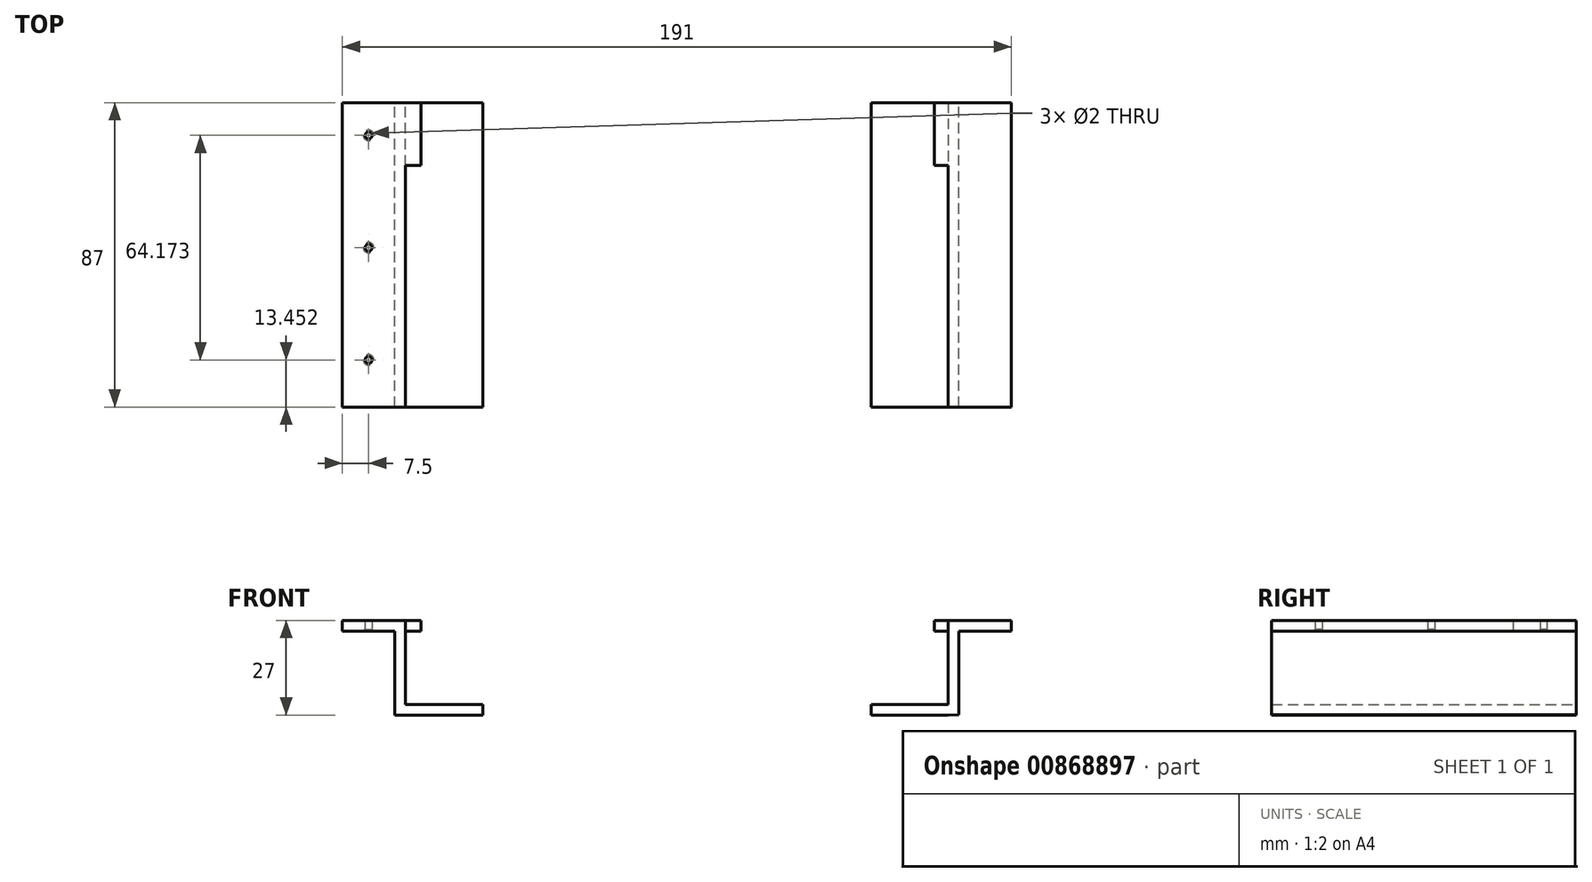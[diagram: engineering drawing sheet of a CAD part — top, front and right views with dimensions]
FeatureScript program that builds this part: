
annotation { "Feature Type Name" : "Feature", "Feature Type Description" : "" }
export const myFeature = defineFeature(function(context is Context, id is Id, definition is map)
    precondition{}
    {
        {
            var Q0;
            Q0=qCreatedBy(makeId("Front.planeOp"),FACE);
            var sketch = newSketch(context, id + "F0", { "sketchPlane" : qUnion([Q0])});
            skLineSegment(sketch, "E0", {"start": v(0, 0) * mm, "end": v(-77.5, 0) * mm});
            skLineSegment(sketch, "E1.bottom", {"start": v(-77.5, 0) * mm, "end": v(77.5, 0) * mm});
            skLineSegment(sketch, "E1.top", {"start": v(-77.5, 24) * mm, "end": v(77.5, 24) * mm});
            skLineSegment(sketch, "E1.left", {"start": v(-77.5, 0) * mm, "end": v(-77.5, 24) * mm});
            skLineSegment(sketch, "E1.right", {"start": v(77.5, 0) * mm, "end": v(77.5, 24) * mm});
            skLineSegment(sketch, "E2", {"start": v(-77.5, 24) * mm, "end": v(-80.5, 24) * mm});
            skLineSegment(sketch, "E3", {"start": v(-80.5, 24) * mm, "end": v(-80.5, 0) * mm});
            skLineSegment(sketch, "E4", {"start": v(-80.5, 0) * mm, "end": v(-80.5, -3) * mm});
            skLineSegment(sketch, "E5", {"start": v(-80.5, -3) * mm, "end": v(77.5, -3) * mm});
            skLineSegment(sketch, "E6", {"start": v(77.5, -3) * mm, "end": v(80.5, -2.98) * mm});
            skLineSegment(sketch, "E7", {"start": v(80.5, -2.98) * mm, "end": v(80.5, 24) * mm});
            skLineSegment(sketch, "E8", {"start": v(80.5, 24) * mm, "end": v(77.5, 24) * mm});
            skLineSegment(sketch, "E9", {"start": v(-80.5, 24) * mm, "end": v(-95.5, 24) * mm});
            skLineSegment(sketch, "E10", {"start": v(-95.5, 24) * mm, "end": v(-95.5, 21) * mm});
            skLineSegment(sketch, "E11", {"start": v(-95.5, 21) * mm, "end": v(-80.5, 21) * mm});
            skLineSegment(sketch, "E12", {"start": v(0, 24) * mm, "end": v(0, -47.67) * mm});
            skLineSegment(sketch, "E13.MirrorCS", {"start": v(77.5, 24) * mm, "end": v(80.5, 24) * mm});
            skLineSegment(sketch, "E14.MirrorCS", {"start": v(95.5, 24) * mm, "end": v(95.5, 21) * mm});
            skLineSegment(sketch, "E15.MirrorCS", {"start": v(80.5, 0) * mm, "end": v(80.5, -3) * mm});
            skLineSegment(sketch, "E16.MirrorCS", {"start": v(80.5, 24) * mm, "end": v(95.5, 24) * mm});
            skLineSegment(sketch, "E17.MirrorCS", {"start": v(80.5, 24) * mm, "end": v(80.5, 0) * mm});
            skLineSegment(sketch, "E18.MirrorCS", {"start": v(95.5, 21) * mm, "end": v(80.5, 21) * mm});
            skLineSegment(sketch, "E19", {"start": v(-77.5, 21) * mm, "end": v(-73, 21) * mm});
            skLineSegment(sketch, "E20", {"start": v(-73, 21) * mm, "end": v(-73, 24) * mm});
            skLineSegment(sketch, "E21", {"start": v(77.5, 21) * mm, "end": v(73.5, 21) * mm});
            skLineSegment(sketch, "E22", {"start": v(73.5, 21) * mm, "end": v(73.5, 24) * mm});
            skLineSegment(sketch, "E23", {"start": v(-95.5, 24) * mm, "end": v(-55.5, 24) * mm});
            skLineSegment(sketch, "E24", {"start": v(-55.44, 24.1) * mm, "end": v(-55.44, -3) * mm});
            skLineSegment(sketch, "E25", {"start": v(95.5, 24) * mm, "end": v(55.5, 24) * mm});
            skLineSegment(sketch, "E26", {"start": v(55.5, 24) * mm, "end": v(55.5, -3) * mm});
            skSolve(sketch);
        }
        {
            var Q0;
            {var subQ4=sQuery(id+"F0.wireOp",EDGE,"E10");Q0=makeQuery(id+"F0.imprint","IMPRINT",FACE,{"disambiguationData":[TD([[makeQuery(id+"F0.imprint","IMPRINT",EDGE,{"derivedFrom":subQ4}),1.0]])]});}
            var Q1;
            {var subQ11=sQuery(id+"F0.wireOp",EDGE,"E4");Q1=makeQuery(id+"F0.imprint","IMPRINT",FACE,{"disambiguationData":[TD([[makeQuery(id+"F0.imprint","IMPRINT",EDGE,{"derivedFrom":subQ11}),1.0]])]});}
            var Q2;
            {var subQ1=sQuery(id+"F0.wireOp",EDGE,"E6");Q2=makeQuery(id+"F0.imprint","IMPRINT",FACE,{"disambiguationData":[TD([[makeQuery(id+"F0.imprint","IMPRINT",EDGE,{"derivedFrom":subQ1}),1.0]])]});}
            var Q3;
            {var subQ0=sQuery(id+"F0.wireOp",EDGE,"E14.MirrorCS");Q3=makeQuery(id+"F0.imprint","IMPRINT",FACE,{"disambiguationData":[TD([[makeQuery(id+"F0.imprint","IMPRINT",EDGE,{"derivedFrom":subQ0}),-1.0]])]});}
            extrude(context, id + "F1", {"entities" : qUnion([Q0, Q1, Q2, Q3]), "depth" : 69 * mm, "offsetDistance" : 25 * mm});
        }
        {
            var Q0;
            {var subQ0=sQuery(id+"F0.wireOp",EDGE,"E14.MirrorCS");Q0=makeQuery(id+"F0.imprint","IMPRINT",FACE,{"disambiguationData":[TD([[makeQuery(id+"F0.imprint","IMPRINT",EDGE,{"derivedFrom":subQ0}),-1.0]])]});}
            var Q1;
            {var subQ3=sQuery(id+"F0.wireOp",EDGE,"E21");Q1=makeQuery(id+"F0.imprint","IMPRINT",FACE,{"disambiguationData":[TD([[makeQuery(id+"F0.imprint","IMPRINT",EDGE,{"derivedFrom":subQ3}),-1.0]])]});}
            var Q2;
            {var subQ1=sQuery(id+"F0.wireOp",EDGE,"E6");Q2=makeQuery(id+"F0.imprint","IMPRINT",FACE,{"disambiguationData":[TD([[makeQuery(id+"F0.imprint","IMPRINT",EDGE,{"derivedFrom":subQ1}),1.0]])]});}
            var Q3;
            {var subQ4=sQuery(id+"F0.wireOp",EDGE,"E10");Q3=makeQuery(id+"F0.imprint","IMPRINT",FACE,{"disambiguationData":[TD([[makeQuery(id+"F0.imprint","IMPRINT",EDGE,{"derivedFrom":subQ4}),1.0]])]});}
            var Q4;
            {var subQ3=sQuery(id+"F0.wireOp",EDGE,"E19");Q4=makeQuery(id+"F0.imprint","IMPRINT",FACE,{"disambiguationData":[TD([[makeQuery(id+"F0.imprint","IMPRINT",EDGE,{"derivedFrom":subQ3}),1.0]])]});}
            var Q5;
            {var subQ11=sQuery(id+"F0.wireOp",EDGE,"E4");Q5=makeQuery(id+"F0.imprint","IMPRINT",FACE,{"disambiguationData":[TD([[makeQuery(id+"F0.imprint","IMPRINT",EDGE,{"derivedFrom":subQ11}),1.0]])]});}
            extrude(context, id + "F2", {"entities" : qUnion([Q0, Q1, Q2, Q3, Q4, Q5]), "operationType" : NewBodyOperationType.ADD, "oppositeDirection" : true, "depth" : 18 * mm, "offsetDistance" : 25 * mm});
        }
        {
            var Q0;
            {var subQ0=sQuery(id+"F0.wireOp",EDGE,"E18.MirrorCS");Q0=makeQuery(id+"F2.boolean.opBoolean","MERGE",FACE,{"derivedFrom":[makeQuery(id+"F1.opExtrude","SWEPT_FACE",FACE,{"disambiguationData":[OSD([subQ0])]}),makeQuery(id+"F2.opExtrude","SWEPT_FACE",FACE,{"disambiguationData":[OSD([subQ0])]})]});}
            var sketch = newSketch(context, id + "F3", { "sketchPlane" : qUnion([Q0])});
            skLineSegment(sketch, "E27.0.0", {"start": v(-95.5, 69) * mm, "end": v(-95.5, -18) * mm});
            skLineSegment(sketch, "E27.0.1", {"start": v(-95.5, -18) * mm, "end": v(-80.5, -18) * mm});
            skLineSegment(sketch, "E27.0.2", {"start": v(-80.5, -18) * mm, "end": v(-80.5, 69) * mm});
            skLineSegment(sketch, "E27.0.3", {"start": v(-80.5, 69) * mm, "end": v(-95.5, 69) * mm});
            skFitSpline(sketch, "E28.0.0", {"points": [v(80.5, 69) * mm, v(80.5, 46) * mm, v(80.5, 23) * mm, v(80.5, 0) * mm]});
            skFitSpline(sketch, "E28.0.1", {"points": [v(80.5, 0) * mm, v(80.5, -6) * mm, v(80.5, -12) * mm, v(80.5, -18) * mm]});
            skLineSegment(sketch, "E28.0.2", {"start": v(80.5, -18) * mm, "end": v(95.5, -18) * mm});
            skLineSegment(sketch, "E28.0.3", {"start": v(95.5, -18) * mm, "end": v(95.5, 69) * mm});
            skLineSegment(sketch, "E28.0.4", {"start": v(95.5, 69) * mm, "end": v(80.5, 69) * mm});
            skFitSpline(sketch, "E29.0.0", {"points": [v(80.5, 69) * mm, v(80.5, 46) * mm, v(80.5, 23) * mm, v(80.5, 0) * mm]});
            skFitSpline(sketch, "E29.0.1", {"points": [v(80.5, 0) * mm, v(80.5, -6) * mm, v(80.5, -12) * mm, v(80.5, -18) * mm]});
            skLineSegment(sketch, "E30", {"start": v(-95.5, 55.55) * mm, "end": v(95.5, 55.55) * mm});
            skLineSegment(sketch, "E31", {"start": v(95.5, 55.55) * mm, "end": v(80.5, 55.55) * mm});
            skLineSegment(sketch, "E32", {"start": v(80.5, 55.55) * mm, "end": v(-80.5, 55.55) * mm});
            skLineSegment(sketch, "E33", {"start": v(-80.5, 55.55) * mm, "end": v(-95.5, 55.55) * mm});
            skLineSegment(sketch, "E34", {"start": v(-88, 55.55) * mm, "end": v(-95.5, 55.55) * mm});
            skLineSegment(sketch, "E35", {"start": v(80.5, 55.55) * mm, "end": v(88, 55.55) * mm});
            skLineSegment(sketch, "E36", {"start": v(-95.5, -8.63) * mm, "end": v(95.5, -8.63) * mm});
            skLineSegment(sketch, "E37", {"start": v(95.5, -8.63) * mm, "end": v(80.5, -8.63) * mm});
            skLineSegment(sketch, "E38", {"start": v(80.5, -8.63) * mm, "end": v(88, -8.63) * mm});
            skLineSegment(sketch, "E39", {"start": v(88, -8.63) * mm, "end": v(-95.5, -8.63) * mm});
            skLineSegment(sketch, "E40", {"start": v(-80.5, -8.63) * mm, "end": v(-95.5, -8.63) * mm});
            skLineSegment(sketch, "E41", {"start": v(-88, -8.63) * mm, "end": v(-95.5, -8.63) * mm});
            skLineSegment(sketch, "E42", {"start": v(-95.5, 55.55) * mm, "end": v(-95.5, -8.63) * mm});
            skLineSegment(sketch, "E43", {"start": v(-95.5, 23.46) * mm, "end": v(95.5, 23.46) * mm});
            skLineSegment(sketch, "E44", {"start": v(95.5, 23.46) * mm, "end": v(80.5, 23.46) * mm});
            skLineSegment(sketch, "E45", {"start": v(80.5, 23.46) * mm, "end": v(88, 23.46) * mm});
            skLineSegment(sketch, "E46", {"start": v(88, 23.46) * mm, "end": v(-95.5, 23.46) * mm});
            skLineSegment(sketch, "E47", {"start": v(-80.5, 23.46) * mm, "end": v(-95.5, 23.46) * mm});
            skLineSegment(sketch, "E48", {"start": v(-95.5, 23.46) * mm, "end": v(-88, 23.46) * mm});
            skSolve(sketch);
        }
        {
            var Q0;
            Q0=sQuery(id+"F3.wireOp",VERTEX,"E35.end");
            var Q1;
            Q1=sQuery(id+"F3.wireOp",VERTEX,"E38.end");
            var Q2;
            Q2=sQuery(id+"F3.wireOp",VERTEX,"E45.end");
            var Q3;
            Q3=sQuery(id+"F3.wireOp",VERTEX,"E34.start");
            var Q4;
            Q4=sQuery(id+"F3.wireOp",VERTEX,"E48.end");
            var Q5;
            Q5=sQuery(id+"F3.wireOp",VERTEX,"E41.start");
            var Q6;
            Q6=makeQuery(id+"F1.opExtrude","SWEPT_BODY",BODY,{"disambiguationData":[OSD([sQuery(id+"F0.wireOp",EDGE,"E1.bottom"),sQuery(id+"F0.wireOp",EDGE,"E1.left"),sQuery(id+"F0.wireOp",EDGE,"E2"),sQuery(id+"F0.wireOp",EDGE,"E3"),sQuery(id+"F0.wireOp",EDGE,"E4"),sQuery(id+"F0.wireOp",EDGE,"E5"),sQuery(id+"F0.wireOp",EDGE,"E6"),sQuery(id+"F0.wireOp",EDGE,"E9"),sQuery(id+"F0.wireOp",EDGE,"E10"),sQuery(id+"F0.wireOp",EDGE,"E11"),sQuery(id+"F0.wireOp",EDGE,"E13.MirrorCS"),sQuery(id+"F0.wireOp",EDGE,"E14.MirrorCS"),sQuery(id+"F0.wireOp",EDGE,"E15.MirrorCS"),sQuery(id+"F0.wireOp",EDGE,"E16.MirrorCS"),sQuery(id+"F0.wireOp",EDGE,"E17.MirrorCS"),sQuery(id+"F0.wireOp",EDGE,"E1.right"),sQuery(id+"F0.wireOp",EDGE,"E18.MirrorCS")])]});
            hole(context, id + "F4", {"style" : HoleStyle.C_SINK, "endStyle" : HoleEndStyle.BLIND, "holeDiameter" : 2 * mm, "cSinkDiameter" : 3 * mm, "cSinkAngle" : 90 * degree, "majorDiameter" : 5 * mm, "holeDepth" : 3 * mm, "isTappedThrough" : true, "tappedDepth" : 12 * mm, "tapClearance" : 3, "locations" : qUnion([Q0, Q1, Q2, Q3, Q4, Q5]), "scope" : qUnion([Q6])});
        }
        {
            var Q0;
            Q0=sQuery(id+"F3.wireOp",VERTEX,"E34.start");
            var Q1;
            Q1=sQuery(id+"F3.wireOp",VERTEX,"E48.end");
            var Q2;
            Q2=sQuery(id+"F3.wireOp",VERTEX,"E41.start");
            var Q3;
            Q3=makeQuery(id+"F1.opExtrude","SWEPT_BODY",BODY,{"disambiguationData":[OSD([sQuery(id+"F0.wireOp",EDGE,"E1.bottom"),sQuery(id+"F0.wireOp",EDGE,"E1.left"),sQuery(id+"F0.wireOp",EDGE,"E3"),sQuery(id+"F0.wireOp",EDGE,"E4"),sQuery(id+"F0.wireOp",EDGE,"E5"),sQuery(id+"F0.wireOp",EDGE,"E10"),sQuery(id+"F0.wireOp",EDGE,"E11"),sQuery(id+"F0.wireOp",EDGE,"E23"),sQuery(id+"F0.wireOp",EDGE,"E24")])]});
            hole(context, id + "F5", {"style" : HoleStyle.C_SINK, "endStyle" : HoleEndStyle.BLIND, "holeDiameter" : 2 * mm, "cSinkDiameter" : 3 * mm, "cSinkAngle" : 90 * degree, "majorDiameter" : 5 * mm, "holeDepth" : 3 * mm, "isTappedThrough" : true, "tappedDepth" : 12 * mm, "tapClearance" : 3, "locations" : qUnion([Q0, Q1, Q2]), "scope" : qUnion([Q3])});
        }
    });
